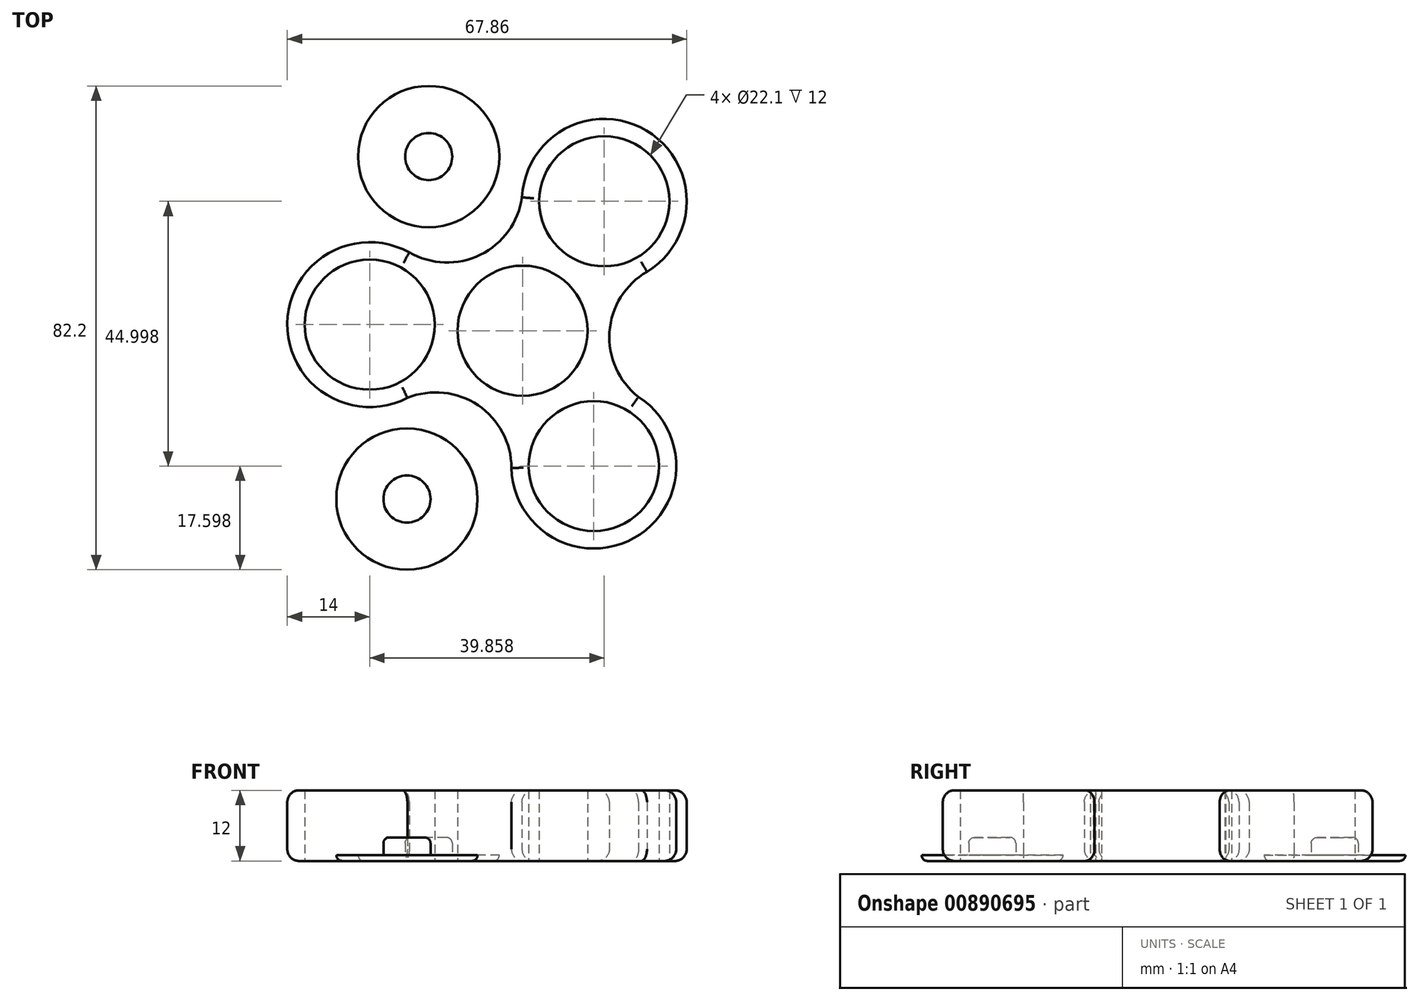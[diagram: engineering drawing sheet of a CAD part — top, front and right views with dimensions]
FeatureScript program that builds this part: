
annotation { "Feature Type Name" : "Feature", "Feature Type Description" : "" }
export const myFeature = defineFeature(function(context is Context, id is Id, definition is map)
    precondition{}
    {
        {
            var Q0;
            Q0=qCreatedBy(makeId("Top.planeOp"),FACE);
            var sketch = newSketch(context, id + "F0", { "sketchPlane" : qUnion([Q0])});
            skCircle(sketch, "E0", {"center": v(0, 0) * mm, "radius": 11.05 * mm});
            skCircle(sketch, "E1.2.0", {"center": v(13.88, 21.99) * mm, "radius": 11.05 * mm});
            skCircle(sketch, "E1.2.1", {"center": v(13.88, 21.99) * mm, "radius": 14 * mm});
            skCircle(sketch, "E2.1.1", {"center": v(-25.98, 1.03) * mm, "radius": 14 * mm});
            skCircle(sketch, "E2.1.2", {"center": v(-25.98, 1.03) * mm, "radius": 11.05 * mm});
            skCircle(sketch, "E2.2.1", {"center": v(12.1, -23.01) * mm, "radius": 14 * mm});
            skCircle(sketch, "E2.2.2", {"center": v(12.1, -23.01) * mm, "radius": 11.05 * mm});
            skArc(sketch, "E3", {"start": v(21.14, 10.02) * mm, "mid": v(14.76, -0.23) * mm, "end": v(19.68, -11.24) * mm});
            skArc(sketch, "E4.1.1", {"start": v(-19.24, 13.3) * mm, "mid": v(-7.18, 12.9) * mm, "end": v(-0.1, 22.67) * mm});
            skArc(sketch, "E4.2.1", {"start": v(-1.9, -23.32) * mm, "mid": v(-7.58, -12.67) * mm, "end": v(-19.58, -11.43) * mm});
            skSolve(sketch);
        }
        {
            var Q0;
            Q0=makeQuery(id+"F0.imprint","IMPRINT",FACE,{"disambiguationData":[TD([[makeQuery(id+"F0.imprint","IMPRINT",EDGE,{"derivedFrom":sQuery(id+"F0.wireOp",EDGE,"E1.2.0")}),-1.0]])]});
            var Q1;
            Q1=makeQuery(id+"F0.imprint","IMPRINT",FACE,{"disambiguationData":[TD([[makeQuery(id+"F0.imprint","IMPRINT",EDGE,{"derivedFrom":sQuery(id+"F0.wireOp",EDGE,"E2.2.2")}),-1.0]])]});
            var Q2;
            Q2=makeQuery(id+"F0.imprint","IMPRINT",FACE,{"disambiguationData":[TD([[makeQuery(id+"F0.imprint","IMPRINT",EDGE,{"derivedFrom":sQuery(id+"F0.wireOp",EDGE,"E2.1.2")}),-1.0]])]});
            var Q3;
            Q3=makeQuery(id+"F0.imprint","IMPRINT",FACE,{"disambiguationData":[TD([[makeQuery(id+"F0.imprint","IMPRINT",EDGE,{"derivedFrom":sQuery(id+"F0.wireOp",EDGE,"E0")}),-1.0]])]});
            extrude(context, id + "F1", {"entities" : qUnion([Q0, Q1, Q2, Q3]), "depth" : 12 * mm, "offsetDistance" : 25 * mm});
        }
        {
            var Q0;
            Q0=makeQuery(id+"F1.opExtrude","CAP_EDGE",EDGE,{"disambiguationData":[OSD([sQuery(id+"F0.wireOp",EDGE,"E4.1.1")])],"isStart":false});
            var Q1;
            Q1=makeQuery(id+"F1.opExtrude","CAP_EDGE",EDGE,{"disambiguationData":[OSD([sQuery(id+"F0.wireOp",EDGE,"E1.2.1")])],"isStart":false});
            var Q2;
            Q2=makeQuery(id+"F1.opExtrude","CAP_EDGE",EDGE,{"disambiguationData":[OSD([sQuery(id+"F0.wireOp",EDGE,"E3")])],"isStart":false});
            var Q3;
            Q3=makeQuery(id+"F1.opExtrude","CAP_EDGE",EDGE,{"disambiguationData":[OSD([sQuery(id+"F0.wireOp",EDGE,"E2.2.1")])],"isStart":false});
            var Q4;
            Q4=makeQuery(id+"F1.opExtrude","CAP_EDGE",EDGE,{"disambiguationData":[OSD([sQuery(id+"F0.wireOp",EDGE,"E4.2.1")])],"isStart":false});
            var Q5;
            Q5=makeQuery(id+"F1.opExtrude","CAP_EDGE",EDGE,{"disambiguationData":[OSD([sQuery(id+"F0.wireOp",EDGE,"E2.1.1")])],"isStart":false});
            var Q6;
            Q6=makeQuery(id+"F1.opExtrude","CAP_EDGE",EDGE,{"disambiguationData":[OSD([sQuery(id+"F0.wireOp",EDGE,"E3")])],"isStart":true});
            var Q7;
            Q7=makeQuery(id+"F1.opExtrude","CAP_EDGE",EDGE,{"disambiguationData":[OSD([sQuery(id+"F0.wireOp",EDGE,"E2.2.1")])],"isStart":true});
            var Q8;
            Q8=makeQuery(id+"F1.opExtrude","CAP_EDGE",EDGE,{"disambiguationData":[OSD([sQuery(id+"F0.wireOp",EDGE,"E4.2.1")])],"isStart":true});
            var Q9;
            Q9=makeQuery(id+"F1.opExtrude","CAP_EDGE",EDGE,{"disambiguationData":[OSD([sQuery(id+"F0.wireOp",EDGE,"E2.1.1")])],"isStart":true});
            var Q10;
            Q10=makeQuery(id+"F1.opExtrude","CAP_EDGE",EDGE,{"disambiguationData":[OSD([sQuery(id+"F0.wireOp",EDGE,"E4.1.1")])],"isStart":true});
            var Q11;
            Q11=makeQuery(id+"F1.opExtrude","CAP_EDGE",EDGE,{"disambiguationData":[OSD([sQuery(id+"F0.wireOp",EDGE,"E1.2.1")])],"isStart":true});
            fillet(context, id + "F2", {"entities" : qUnion([Q0, Q1, Q2, Q3, Q4, Q5, Q6, Q7, Q8, Q9, Q10, Q11]), "radius" : 2 * mm, "tangentPropagation" : true, "allowEdgeOverflow" : false});
        }
        {
            var Q0;
            Q0=qCreatedBy(makeId("Top.planeOp"),FACE);
            var sketch = newSketch(context, id + "F3", { "sketchPlane" : qUnion([Q0])});
            skCircle(sketch, "E5", {"center": v(-19.65, -28.61) * mm, "radius": 4 * mm});
            skCircle(sketch, "E6", {"center": v(-19.65, -28.61) * mm, "radius": 12 * mm});
            skSolve(sketch);
        }
        {
            var Q0;
            Q0=qCreatedBy(makeId("Top.planeOp"),FACE);
            var sketch = newSketch(context, id + "F4", { "sketchPlane" : qUnion([Q0])});
            skCircle(sketch, "E7", {"center": v(-15.96, 29.59) * mm, "radius": 4 * mm});
            skCircle(sketch, "E8", {"center": v(-15.96, 29.59) * mm, "radius": 12 * mm});
            skSolve(sketch);
        }
        {
            var Q0;
            Q0=makeQuery(id+"F3.imprint","IMPRINT",FACE,{"disambiguationData":[TD([[makeQuery(id+"F3.imprint","IMPRINT",EDGE,{"derivedFrom":sQuery(id+"F3.wireOp",EDGE,"E5")}),1.0]])]});
            extrude(context, id + "F5", {"entities" : qUnion([Q0]), "depth" : 4 * mm, "offsetDistance" : 25 * mm});
        }
        {
            var Q0;
            Q0=makeQuery(id+"F3.imprint","IMPRINT",FACE,{"disambiguationData":[TD([[makeQuery(id+"F3.imprint","IMPRINT",EDGE,{"derivedFrom":sQuery(id+"F3.wireOp",EDGE,"E5")}),-1.0]])]});
            extrude(context, id + "F6", {"entities" : qUnion([Q0]), "operationType" : NewBodyOperationType.ADD, "depth" : 1 * mm, "offsetDistance" : 25 * mm});
        }
        {
            var Q0;
            Q0=makeQuery(id+"F6.opExtrude","CAP_EDGE",EDGE,{"disambiguationData":[OSD([sQuery(id+"F3.wireOp",EDGE,"E6")])],"isStart":true});
            var Q1;
            Q1=makeQuery(id+"F6.opExtrude","CAP_EDGE",EDGE,{"disambiguationData":[OSD([sQuery(id+"F4.wireOp",EDGE,"E8")])],"isStart":true});
            var Q2;
            Q2=makeQuery(id+"F5.opExtrude","CAP_EDGE",EDGE,{"disambiguationData":[OSD([sQuery(id+"F3.wireOp",EDGE,"E5")])],"isStart":false});
            fillet(context, id + "F7", {"entities" : qUnion([Q0, Q1, Q2]), "radius" : 1 * mm, "tangentPropagation" : true, "allowEdgeOverflow" : false});
        }
        {
            var Q0;
            Q0=makeQuery(id+"F4.imprint","IMPRINT",FACE,{"disambiguationData":[TD([[makeQuery(id+"F4.imprint","IMPRINT",EDGE,{"derivedFrom":sQuery(id+"F4.wireOp",EDGE,"E7")}),1.0]])]});
            extrude(context, id + "F8", {"entities" : qUnion([Q0]), "depth" : 4 * mm, "offsetDistance" : 25 * mm});
        }
        {
            var Q0;
            Q0=makeQuery(id+"F4.imprint","IMPRINT",FACE,{"disambiguationData":[TD([[makeQuery(id+"F4.imprint","IMPRINT",EDGE,{"derivedFrom":sQuery(id+"F4.wireOp",EDGE,"E7")}),-1.0]])]});
            extrude(context, id + "F9", {"entities" : qUnion([Q0]), "operationType" : NewBodyOperationType.ADD, "depth" : 1 * mm, "offsetDistance" : 25 * mm});
        }
        {
            var Q0;
            Q0=makeQuery(id+"F9.opExtrude","CAP_EDGE",EDGE,{"disambiguationData":[OSD([sQuery(id+"F4.wireOp",EDGE,"E8")])],"isStart":true});
            var Q1;
            Q1=makeQuery(id+"F8.opExtrude","CAP_EDGE",EDGE,{"disambiguationData":[OSD([sQuery(id+"F4.wireOp",EDGE,"E7")])],"isStart":false});
            fillet(context, id + "F10", {"entities" : qUnion([Q0, Q1]), "radius" : 1 * mm, "tangentPropagation" : true, "allowEdgeOverflow" : false});
        }
    });
